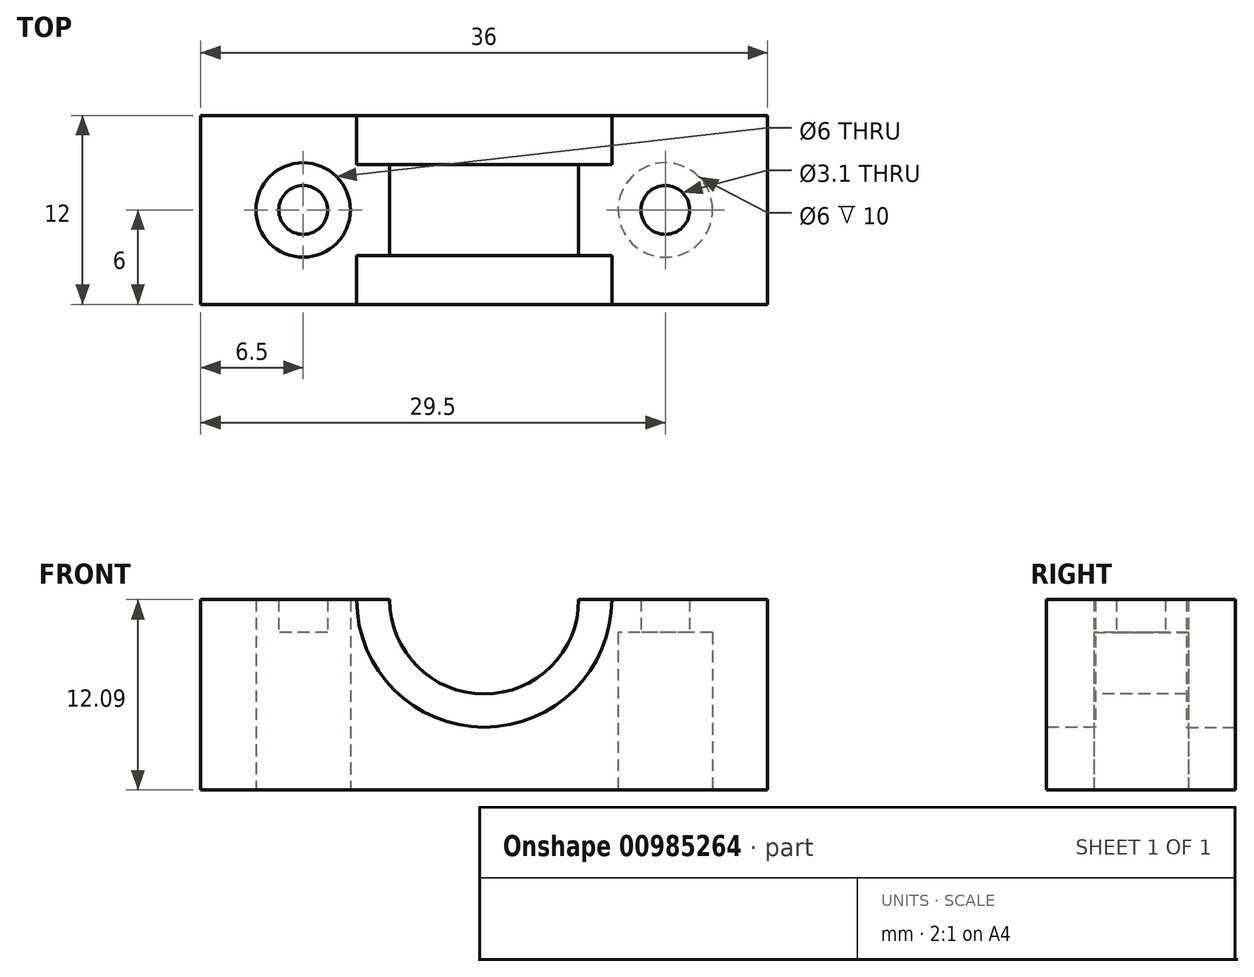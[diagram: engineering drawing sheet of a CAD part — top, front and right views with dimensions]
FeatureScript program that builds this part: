
annotation { "Feature Type Name" : "Feature", "Feature Type Description" : "" }
export const myFeature = defineFeature(function(context is Context, id is Id, definition is map)
    precondition{}
    {
        {
            var Q0;
            Q0=qCreatedBy(makeId("Top.planeOp"),FACE);
            var sketch = newSketch(context, id + "F0", { "sketchPlane" : qUnion([Q0])});
            skLineSegment(sketch, "E0.bottom", {"start": v(18, -6) * mm, "end": v(-18, -6) * mm});
            skLineSegment(sketch, "E0.top", {"start": v(18, 6) * mm, "end": v(-18, 6) * mm});
            skLineSegment(sketch, "E0.left", {"start": v(18, -6) * mm, "end": v(18, 6) * mm});
            skLineSegment(sketch, "E0.right", {"start": v(-18, -6) * mm, "end": v(-18, 6) * mm});
            skPoint(sketch, "E0.middle", {"position": v(0, 0) * mm});
            skLineSegment(sketch, "E1", {"start": v(-18, 0) * mm, "end": v(18, 0) * mm, "construction": true});
            skCircle(sketch, "E2", {"center": v(11.5, 0) * mm, "radius": 1.55 * mm});
            skLineSegment(sketch, "E3", {"start": v(11.5, 6) * mm, "end": v(11.5, -6) * mm, "construction": true});
            skLineSegment(sketch, "E4", {"start": v(0, 6) * mm, "end": v(0, -6) * mm, "construction": true});
            skCircle(sketch, "E5.MirrorC", {"center": v(-11.5, 0) * mm, "radius": 1.55 * mm});
            skCircle(sketch, "E6", {"center": v(11.5, 0) * mm, "radius": 3 * mm});
            skCircle(sketch, "E7.MirrorC", {"center": v(-11.5, 0) * mm, "radius": 3 * mm});
            skSolve(sketch);
        }
        {
            var Q0;
            Q0=makeQuery(id+"F0.imprint","IMPRINT",FACE,{"disambiguationData":[TD([[makeQuery(id+"F0.imprint","IMPRINT",EDGE,{"derivedFrom":sQuery(id+"F0.wireOp",EDGE,"E0.bottom")}),-1.0]])]});
            var Q1;
            Q1=makeQuery(id+"F0.imprint","IMPRINT",FACE,{"disambiguationData":[TD([[makeQuery(id+"F0.imprint","IMPRINT",EDGE,{"derivedFrom":sQuery(id+"F0.wireOp",EDGE,"E2")}),-1.0]])]});
            var Q2;
            Q2=makeQuery(id+"F0.imprint","IMPRINT",FACE,{"disambiguationData":[TD([[makeQuery(id+"F0.imprint","IMPRINT",EDGE,{"derivedFrom":sQuery(id+"F0.wireOp",EDGE,"E5.MirrorC")}),1.0]])]});
            extrude(context, id + "F1", {"entities" : qUnion([Q0, Q1, Q2]), "depth" : 12.1 * mm, "offsetDistance" : 25 * mm});
        }
        {
            var Q0;
            Q0=makeQuery(id+"F0.imprint","IMPRINT",FACE,{"disambiguationData":[TD([[makeQuery(id+"F0.imprint","IMPRINT",EDGE,{"derivedFrom":sQuery(id+"F0.wireOp",EDGE,"E5.MirrorC")}),1.0]])]});
            var Q1;
            Q1=makeQuery(id+"F0.imprint","IMPRINT",FACE,{"disambiguationData":[TD([[makeQuery(id+"F0.imprint","IMPRINT",EDGE,{"derivedFrom":sQuery(id+"F0.wireOp",EDGE,"E2")}),-1.0]])]});
            extrude(context, id + "F2", {"entities" : qUnion([Q0, Q1]), "operationType" : NewBodyOperationType.REMOVE, "depth" : 10 * mm, "offsetDistance" : 25 * mm});
        }
        {
            var Q0;
            Q0=makeQuery(id+"F1.opExtrude","SWEPT_FACE",FACE,{"disambiguationData":[OSD([sQuery(id+"F0.wireOp",EDGE,"E0.bottom")])]});
            var sketch = newSketch(context, id + "F3", { "sketchPlane" : qUnion([Q0])});
            skArc(sketch, "E8", {"start": v(-8.1, 12.1) * mm, "mid": v(0, 3.99) * mm, "end": v(8.1, 12.09) * mm});
            skArc(sketch, "E9", {"start": v(-6, 12.1) * mm, "mid": v(0, 6.09) * mm, "end": v(6, 12.1) * mm});
            skPoint(sketch, "E10", {"position": v(-6, 12.1) * mm});
            skPoint(sketch, "E11", {"position": v(-8.1, 12.1) * mm});
            skPoint(sketch, "E12", {"position": v(6, 12.1) * mm});
            skPoint(sketch, "E13", {"position": v(8.1, 12.1) * mm});
            skSolve(sketch);
        }
        {
            var Q0;
            {var subQ0=sQuery(id+"F3.wireOp",EDGE,"E9");Q0=makeQuery(id+"F3.imprint","IMPRINT",FACE,{"disambiguationData":[TD([[makeQuery(id+"F3.imprint","IMPRINT",EDGE,{"derivedFrom":subQ0}),1.0]])]});}
            extrude(context, id + "F4", {"entities" : qUnion([Q0]), "operationType" : NewBodyOperationType.REMOVE, "endBound" : BoundingType.UP_TO_NEXT, "oppositeDirection" : true, "depth" : 25 * mm, "offsetDistance" : 25 * mm});
        }
        {
            var Q0;
            {var subQ0=sQuery(id+"F3.wireOp",EDGE,"E8");Q0=makeQuery(id+"F3.imprint","IMPRINT",FACE,{"disambiguationData":[TD([[makeQuery(id+"F3.imprint","IMPRINT",EDGE,{"derivedFrom":subQ0}),1.0]])]});}
            extrude(context, id + "F5", {"entities" : qUnion([Q0]), "operationType" : NewBodyOperationType.REMOVE, "oppositeDirection" : true, "depth" : 3.1 * mm, "offsetDistance" : 25 * mm});
        }
        {
            var Q0;
            Q0=makeQuery(id+"F1.opExtrude","SWEPT_FACE",FACE,{"disambiguationData":[OSD([sQuery(id+"F0.wireOp",EDGE,"E0.top")])]});
            var sketch = newSketch(context, id + "F6", { "sketchPlane" : qUnion([Q0])});
            skArc(sketch, "E14", {"start": v(-8.1, 12.09) * mm, "mid": v(0, 3.99) * mm, "end": v(8.1, 12.1) * mm});
            skArc(sketch, "E15", {"start": v(-6, 12.1) * mm, "mid": v(0, 6.09) * mm, "end": v(6, 12.1) * mm});
            skPoint(sketch, "E16", {"position": v(-6, 12.1) * mm});
            skPoint(sketch, "E17", {"position": v(-8.1, 12.1) * mm});
            skPoint(sketch, "E18", {"position": v(6, 12.1) * mm});
            skPoint(sketch, "E19", {"position": v(8.1, 12.1) * mm});
            skSolve(sketch);
        }
        {
            var Q0;
            {var subQ0=sQuery(id+"F6.wireOp",EDGE,"E14");Q0=makeQuery(id+"F6.imprint","IMPRINT",FACE,{"disambiguationData":[TD([[makeQuery(id+"F6.imprint","IMPRINT",EDGE,{"derivedFrom":subQ0}),1.0]])]});}
            extrude(context, id + "F7", {"entities" : qUnion([Q0]), "operationType" : NewBodyOperationType.REMOVE, "oppositeDirection" : true, "depth" : 3.1 * mm, "offsetDistance" : 25 * mm});
        }
    });
